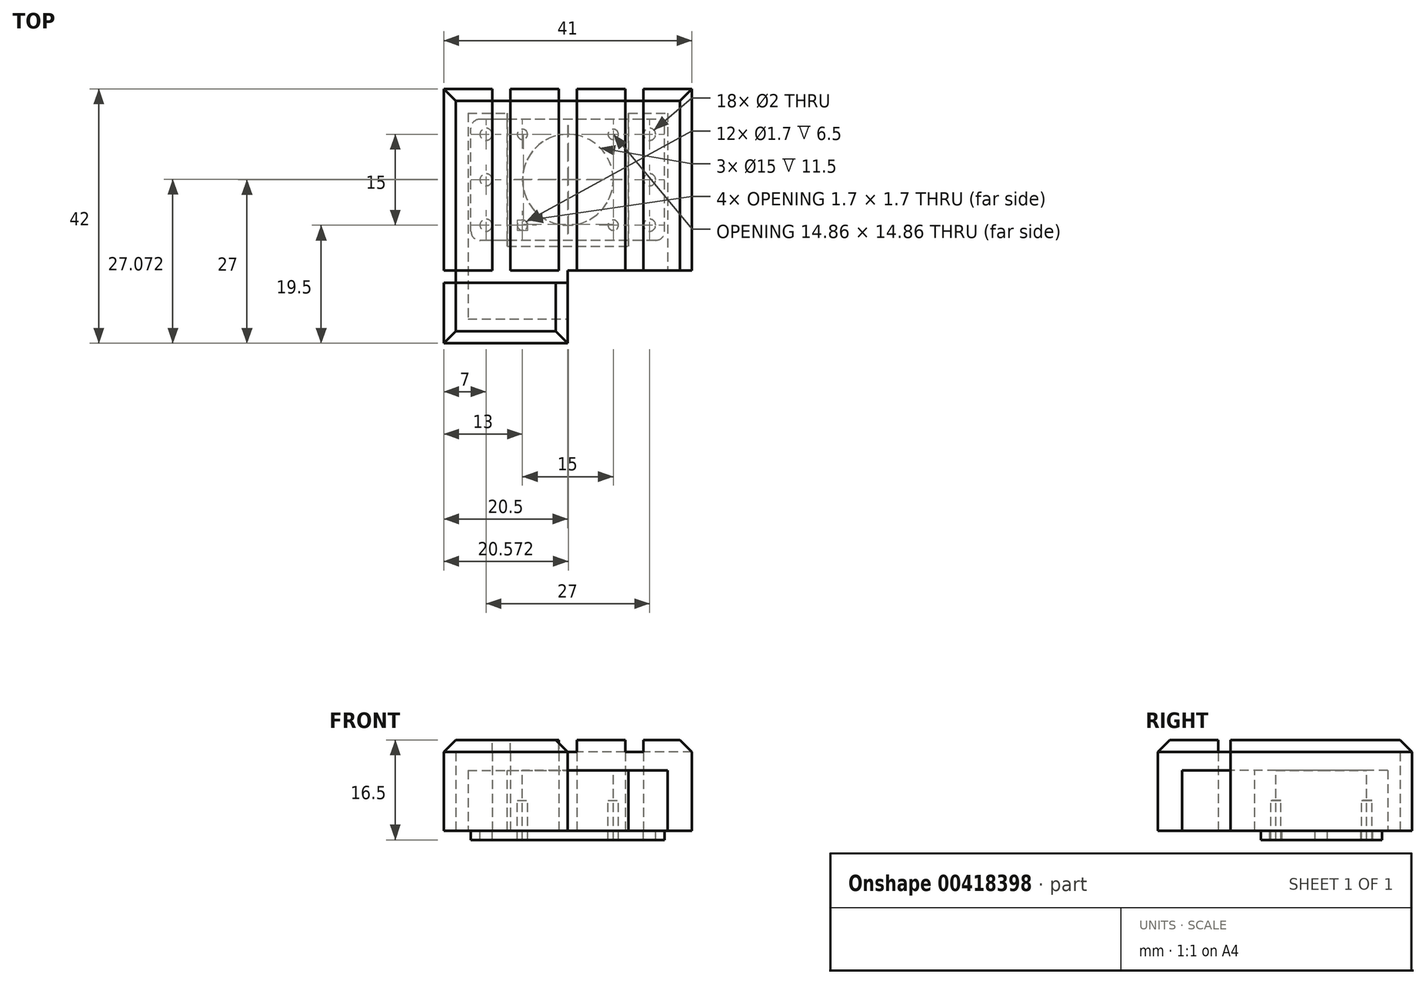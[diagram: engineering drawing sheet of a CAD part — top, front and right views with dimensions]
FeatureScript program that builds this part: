
annotation { "Feature Type Name" : "Feature", "Feature Type Description" : "" }
export const myFeature = defineFeature(function(context is Context, id is Id, definition is map)
    precondition{}
    {
        {
            var Q0;
            Q0=qCreatedBy(makeId("Top.planeOp"),FACE);
            var sketch = newSketch(context, id + "F0", { "sketchPlane" : qUnion([Q0])});
            skLineSegment(sketch, "E0.bottom", {"start": v(-20.5, 15) * mm, "end": v(20.5, 15) * mm});
            skLineSegment(sketch, "E0.top", {"start": v(-20.5, -15) * mm, "end": v(20.5, -15) * mm});
            skLineSegment(sketch, "E0.left", {"start": v(-20.5, 15) * mm, "end": v(-20.5, -15) * mm});
            skLineSegment(sketch, "E0.right", {"start": v(20.5, 15) * mm, "end": v(20.5, -15) * mm});
            skPoint(sketch, "E0.middle", {"position": v(0, 0) * mm});
            skLineSegment(sketch, "E1", {"start": v(-12.5, 15) * mm, "end": v(-12.5, -15) * mm});
            skLineSegment(sketch, "E2", {"start": v(-9.5, 15) * mm, "end": v(-9.5, -15) * mm});
            skLineSegment(sketch, "E3.MirrorCS", {"start": v(12.5, 15) * mm, "end": v(12.5, -15) * mm});
            skLineSegment(sketch, "E4.MirrorCS", {"start": v(9.5, 15) * mm, "end": v(9.5, -15) * mm});
            skLineSegment(sketch, "E5", {"start": v(-1.5, 15) * mm, "end": v(-1.5, -15) * mm});
            skLineSegment(sketch, "E6.MirrorCS", {"start": v(1.5, 15) * mm, "end": v(1.5, -15) * mm});
            skLineSegment(sketch, "E7", {"start": v(0, -15) * mm, "end": v(0, -27) * mm});
            skLineSegment(sketch, "E8", {"start": v(0, -27) * mm, "end": v(20.5, -27) * mm});
            skLineSegment(sketch, "E9", {"start": v(20.5, -27) * mm, "end": v(20.5, -15) * mm});
            skLineSegment(sketch, "E10", {"start": v(0, -17) * mm, "end": v(20.5, -17) * mm});
            skSolve(sketch);
        }
        {
            var Q0;
            Q0=qSketchRegion(id+"F0",true);
            extrude(context, id + "F1", {"entities" : qUnion([Q0]), "oppositeDirection" : true, "depth" : 15 * mm, "offsetDistance" : 25 * mm});
        }
        {
            var Q0;
            {var subQ0=sQuery(id+"F0.wireOp",EDGE,"E1");Q0=makeQuery(id+"F0.imprint","IMPRINT",FACE,{"disambiguationData":[TD([[makeQuery(id+"F0.imprint","IMPRINT",EDGE,{"derivedFrom":subQ0}),1.0]])]});}
            var Q1;
            {var subQ0=sQuery(id+"F0.wireOp",EDGE,"E5");Q1=makeQuery(id+"F0.imprint","IMPRINT",FACE,{"disambiguationData":[TD([[makeQuery(id+"F0.imprint","IMPRINT",EDGE,{"derivedFrom":subQ0}),1.0]])]});}
            var Q2;
            {var subQ0=sQuery(id+"F0.wireOp",EDGE,"E3.MirrorCS");Q2=makeQuery(id+"F0.imprint","IMPRINT",FACE,{"disambiguationData":[TD([[makeQuery(id+"F0.imprint","IMPRINT",EDGE,{"derivedFrom":subQ0}),-1.0]])]});}
            var Q3;
            {var subQ8=sQuery(id+"F0.wireOp",EDGE,"E10");Q3=makeQuery(id+"F0.imprint","IMPRINT",FACE,{"disambiguationData":[TD([[makeQuery(id+"F0.imprint","IMPRINT",EDGE,{"derivedFrom":subQ8}),1.0]])]});}
            extrude(context, id + "F2", {"entities" : qUnion([Q0, Q1, Q2, Q3]), "operationType" : NewBodyOperationType.REMOVE, "oppositeDirection" : true, "depth" : 2 * mm, "offsetDistance" : 25 * mm});
        }
        {
            var Q0;
            {var subQ0=sQuery(id+"F0.wireOp",EDGE,"E0.bottom");var subQ1=sQuery(id+"F0.wireOp",EDGE,"E0.left");Q0=makeQuery(id+"F2.boolean.opBoolean","SPLIT",EDGE,{"disambiguationData":[TD([makeQuery(id+"F1.opExtrude","SWEPT_FACE",FACE,{"disambiguationData":[OSD([subQ1])]})])],"derivedFrom":makeQuery(id+"F1.opExtrude","CAP_EDGE",EDGE,{"disambiguationData":[OSD([subQ0])],"isStart":true})});}
            var Q1;
            Q1=makeQuery(id+"F1.opExtrude","CAP_EDGE",EDGE,{"disambiguationData":[OSD([sQuery(id+"F0.wireOp",EDGE,"E0.left")])],"isStart":true});
            var Q2;
            {var subQ0=sQuery(id+"F0.wireOp",EDGE,"E0.bottom");var subQ1=sQuery(id+"F0.wireOp",EDGE,"E9");var subQ2=sQuery(id+"F0.wireOp",EDGE,"E0.right");Q2=makeQuery(id+"F2.boolean.opBoolean","SPLIT",EDGE,{"disambiguationData":[TD([makeQuery(id+"F1.opExtrude","SWEPT_FACE",FACE,{"disambiguationData":[OSD([subQ0])]})])],"derivedFrom":makeQuery(id+"F1.opExtrude","CAP_EDGE",EDGE,{"disambiguationData":[OSD([subQ2,subQ1])],"isStart":true})});}
            var Q3;
            {var subQ0=sQuery(id+"F0.wireOp",EDGE,"E0.bottom");Q3=makeQuery(id+"F2.boolean.opBoolean","SPLIT",EDGE,{"disambiguationData":[TD([makeQuery(id+"F2.opExtrude","SWEPT_FACE",FACE,{"disambiguationData":[OSD([sQuery(id+"F0.wireOp",EDGE,"E3.MirrorCS")])]})])],"derivedFrom":makeQuery(id+"F1.opExtrude","CAP_EDGE",EDGE,{"disambiguationData":[OSD([subQ0])],"isStart":true})});}
            var Q4;
            {var subQ0=sQuery(id+"F0.wireOp",EDGE,"E0.bottom");Q4=makeQuery(id+"F2.boolean.opBoolean","SPLIT",EDGE,{"disambiguationData":[TD([makeQuery(id+"F2.opExtrude","SWEPT_FACE",FACE,{"disambiguationData":[OSD([sQuery(id+"F0.wireOp",EDGE,"E4.MirrorCS")])]})])],"derivedFrom":makeQuery(id+"F1.opExtrude","CAP_EDGE",EDGE,{"disambiguationData":[OSD([subQ0])],"isStart":true})});}
            var Q5;
            {var subQ0=sQuery(id+"F0.wireOp",EDGE,"E0.bottom");Q5=makeQuery(id+"F2.boolean.opBoolean","SPLIT",EDGE,{"disambiguationData":[TD([makeQuery(id+"F2.opExtrude","SWEPT_FACE",FACE,{"disambiguationData":[OSD([sQuery(id+"F0.wireOp",EDGE,"E2")])]})])],"derivedFrom":makeQuery(id+"F1.opExtrude","CAP_EDGE",EDGE,{"disambiguationData":[OSD([subQ0])],"isStart":true})});}
            var Q6;
            Q6=makeQuery(id+"F1.opExtrude","CAP_EDGE",EDGE,{"disambiguationData":[OSD([sQuery(id+"F0.wireOp",EDGE,"E8")])],"isStart":true});
            var Q7;
            {var subQ0=sQuery(id+"F0.wireOp",EDGE,"E9");var subQ1=sQuery(id+"F0.wireOp",EDGE,"E8");var subQ2=sQuery(id+"F0.wireOp",EDGE,"E0.right");Q7=makeQuery(id+"F2.boolean.opBoolean","SPLIT",EDGE,{"disambiguationData":[TD([makeQuery(id+"F1.opExtrude","SWEPT_FACE",FACE,{"disambiguationData":[OSD([subQ1])]})])],"derivedFrom":makeQuery(id+"F1.opExtrude","CAP_EDGE",EDGE,{"disambiguationData":[OSD([subQ2,subQ0])],"isStart":true})});}
            var Q8;
            Q8=makeQuery(id+"F1.opExtrude","CAP_EDGE",EDGE,{"disambiguationData":[OSD([sQuery(id+"F0.wireOp",EDGE,"E7")])],"isStart":true});
            chamfer(context, id + "F3", {"entities" : qUnion([Q0, Q1, Q2, Q3, Q4, Q5, Q6, Q7, Q8]), "width" : 2 * mm, "tangentPropagation" : true});
        }
        {
            var Q0;
            {var subQ0=sQuery(id+"F0.wireOp",EDGE,"E0.bottom");var subQ1=sQuery(id+"F0.wireOp",EDGE,"E4.MirrorCS");var subQ2=sQuery(id+"F0.wireOp",EDGE,"E0.top");Q0=makeQuery(id+"F2.boolean.opBoolean","SPLIT",FACE,{"disambiguationData":[TD([makeQuery(id+"F2.opExtrude","SWEPT_FACE",FACE,{"disambiguationData":[OSD([subQ1])]})])],"derivedFrom":makeQuery(id+"F1.opExtrude","CAP_FACE",FACE,{"disambiguationData":[OSD([subQ0,subQ2,sQuery(id+"F0.wireOp",EDGE,"E0.left"),sQuery(id+"F0.wireOp",EDGE,"E0.right"),sQuery(id+"F0.wireOp",EDGE,"E7"),sQuery(id+"F0.wireOp",EDGE,"E8"),sQuery(id+"F0.wireOp",EDGE,"E9")])],"isStart":true})});}
            var sketch = newSketch(context, id + "F4", { "sketchPlane" : qUnion([Q0])});
            skCircle(sketch, "E11", {"center": v(-7.5, 7.5) * mm, "radius": 0.85 * mm});
            skCircle(sketch, "E12.MirrorC", {"center": v(7.5, 7.5) * mm, "radius": 0.85 * mm});
            skCircle(sketch, "E13.MirrorC", {"center": v(7.5, -7.5) * mm, "radius": 0.85 * mm});
            skCircle(sketch, "E14.MirrorC", {"center": v(-7.5, -7.5) * mm, "radius": 0.85 * mm});
            skSolve(sketch);
        }
        {
            var Q0;
            Q0=qSketchRegion(id+"F4",true);
            extrude(context, id + "F5", {"entities" : qUnion([Q0]), "operationType" : NewBodyOperationType.REMOVE, "endBound" : BoundingType.THROUGH_ALL, "oppositeDirection" : true, "depth" : 25 * mm, "offsetDistance" : 25 * mm});
        }
        {
            var Q0;
            Q0=makeQuery(id+"F1.opExtrude","CAP_FACE",FACE,{"disambiguationData":[OSD([sQuery(id+"F0.wireOp",EDGE,"E0.bottom"),sQuery(id+"F0.wireOp",EDGE,"E0.top"),sQuery(id+"F0.wireOp",EDGE,"E0.left"),sQuery(id+"F0.wireOp",EDGE,"E0.right"),sQuery(id+"F0.wireOp",EDGE,"E7"),sQuery(id+"F0.wireOp",EDGE,"E8"),sQuery(id+"F0.wireOp",EDGE,"E9")])],"isStart":false});
            var sketch = newSketch(context, id + "F6", { "sketchPlane" : qUnion([Q0])});
            skLineSegment(sketch, "E15.bottom", {"start": v(8.5, 16) * mm, "end": v(-8.5, 16) * mm});
            skLineSegment(sketch, "E15.top", {"start": v(8.5, -16) * mm, "end": v(-8.5, -16) * mm});
            skLineSegment(sketch, "E15.left", {"start": v(10, 14.5) * mm, "end": v(10, -14.5) * mm});
            skLineSegment(sketch, "E15.right", {"start": v(-10, 14.5) * mm, "end": v(-10, -14.5) * mm});
            skPoint(sketch, "E15.middle", {"position": v(0, 0) * mm});
            skCircle(sketch, "E16", {"center": v(0, 13.5) * mm, "radius": 1 * mm});
            skCircle(sketch, "E17", {"center": v(7.5, 13.5) * mm, "radius": 1 * mm});
            skCircle(sketch, "E18.MirrorC", {"center": v(-7.5, 13.5) * mm, "radius": 1 * mm});
            skCircle(sketch, "E19.MirrorC", {"center": v(7.5, -13.5) * mm, "radius": 1 * mm});
            skCircle(sketch, "E20.MirrorC", {"center": v(-7.5, -13.5) * mm, "radius": 1 * mm});
            skCircle(sketch, "E21.MirrorC", {"center": v(0, -13.5) * mm, "radius": 1 * mm});
            skPoint(sketch, "E22.visualSharp", {"position": v(10, 16) * mm});
            skArc(sketch, "E22.filletArc", {"start": v(10, 14.5) * mm, "mid": v(9.56, 15.56) * mm, "end": v(8.5, 16) * mm});
            skPoint(sketch, "E23.visualSharp", {"position": v(10, -16) * mm});
            skArc(sketch, "E23.filletArc", {"start": v(8.5, -16) * mm, "mid": v(9.56, -15.56) * mm, "end": v(10, -14.5) * mm});
            skPoint(sketch, "E24.visualSharp", {"position": v(-10, -16) * mm});
            skArc(sketch, "E24.filletArc", {"start": v(-10, -14.5) * mm, "mid": v(-9.56, -15.56) * mm, "end": v(-8.5, -16) * mm});
            skPoint(sketch, "E25.visualSharp", {"position": v(-10, 16) * mm});
            skArc(sketch, "E25.filletArc", {"start": v(-8.5, 16) * mm, "mid": v(-9.56, 15.56) * mm, "end": v(-10, 14.5) * mm});
            skCircle(sketch, "E26", {"center": v(0, 0) * mm, "radius": 7.5 * mm});
            skSolve(sketch);
        }
        {
            var Q0;
            Q0=qSketchRegion(id+"F6",true);
            extrude(context, id + "F7", {"entities" : qUnion([Q0]), "depth" : 1.5 * mm, "offsetDistance" : 25 * mm});
        }
        {
            var Q0;
            Q0=makeQuery(id+"F1.opExtrude","SWEPT_FACE",FACE,{"disambiguationData":[OSD([sQuery(id+"F0.wireOp",EDGE,"E0.bottom")])]});
            var sketch = newSketch(context, id + "F8", { "sketchPlane" : qUnion([Q0])});
            skLineSegment(sketch, "E27", {"start": v(12.5, -2) * mm, "end": v(12.5, -15) * mm});
            skLineSegment(sketch, "E28", {"start": v(9.5, -2) * mm, "end": v(9.5, -15) * mm});
            skLineSegment(sketch, "E29", {"start": v(9.5, -15) * mm, "end": v(12.5, -15) * mm});
            skLineSegment(sketch, "E30", {"start": v(12.5, -2) * mm, "end": v(9.5, -2) * mm});
            skLineSegment(sketch, "E31", {"start": v(1.5, -2) * mm, "end": v(1.5, -15) * mm});
            skLineSegment(sketch, "E32", {"start": v(1.5, -15) * mm, "end": v(0, -15) * mm});
            skLineSegment(sketch, "E33", {"start": v(1.5, -2) * mm, "end": v(0, -2) * mm});
            skLineSegment(sketch, "E34.MirrorCS", {"start": v(-1.5, -2) * mm, "end": v(0, -2) * mm});
            skLineSegment(sketch, "E35.MirrorCS", {"start": v(-1.5, -15) * mm, "end": v(0, -15) * mm});
            skLineSegment(sketch, "E36.MirrorCS", {"start": v(-9.5, -15) * mm, "end": v(-12.5, -15) * mm});
            skLineSegment(sketch, "E37.MirrorCS", {"start": v(-12.5, -2) * mm, "end": v(-12.5, -15) * mm});
            skLineSegment(sketch, "E38.MirrorCS", {"start": v(-1.5, -2) * mm, "end": v(-1.5, -15) * mm});
            skLineSegment(sketch, "E39.MirrorCS", {"start": v(-12.5, -2) * mm, "end": v(-9.5, -2) * mm});
            skLineSegment(sketch, "E40.MirrorCS", {"start": v(-9.5, -2) * mm, "end": v(-9.5, -15) * mm});
            skSolve(sketch);
        }
        {
            var Q0;
            Q0=qSketchRegion(id+"F8",true);
            extrude(context, id + "F9", {"entities" : qUnion([Q0]), "operationType" : NewBodyOperationType.REMOVE, "oppositeDirection" : true, "depth" : 2 * mm, "offsetDistance" : 25 * mm});
        }
        {
            var Q0;
            Q0=makeQuery(id+"F1.opExtrude","SWEPT_FACE",FACE,{"disambiguationData":[OSD([sQuery(id+"F0.wireOp",EDGE,"E0.right"),sQuery(id+"F0.wireOp",EDGE,"E9")])]});
            var sketch = newSketch(context, id + "F10", { "sketchPlane" : qUnion([Q0])});
            skLineSegment(sketch, "E41.bottom", {"start": v(-15, -2) * mm, "end": v(-17, -2) * mm});
            skLineSegment(sketch, "E41.top", {"start": v(-15, -15) * mm, "end": v(-17, -15) * mm});
            skLineSegment(sketch, "E41.left", {"start": v(-15, -2) * mm, "end": v(-15, -15) * mm});
            skLineSegment(sketch, "E41.right", {"start": v(-17, -2) * mm, "end": v(-17, -15) * mm});
            skSolve(sketch);
        }
        {
            var Q0;
            Q0=qSketchRegion(id+"F10",true);
            extrude(context, id + "F11", {"entities" : qUnion([Q0]), "operationType" : NewBodyOperationType.REMOVE, "oppositeDirection" : true, "depth" : 2 * mm, "offsetDistance" : 25 * mm});
        }
        {
            var Q0;
            Q0=makeQuery(id+"F7.opExtrude","SWEPT_BODY",BODY,{"disambiguationData":[OSD([sQuery(id+"F6.wireOp",EDGE,"E15.bottom"),sQuery(id+"F6.wireOp",EDGE,"E15.top"),sQuery(id+"F6.wireOp",EDGE,"E15.left"),sQuery(id+"F6.wireOp",EDGE,"E15.right"),sQuery(id+"F6.wireOp",EDGE,"E16"),sQuery(id+"F6.wireOp",EDGE,"E18.MirrorC"),sQuery(id+"F6.wireOp",EDGE,"E17"),sQuery(id+"F6.wireOp",EDGE,"E19.MirrorC"),sQuery(id+"F6.wireOp",EDGE,"E20.MirrorC"),sQuery(id+"F6.wireOp",EDGE,"E21.MirrorC"),sQuery(id+"F6.wireOp",EDGE,"E22.filletArc"),sQuery(id+"F6.wireOp",EDGE,"E23.filletArc"),sQuery(id+"F6.wireOp",EDGE,"E24.filletArc"),sQuery(id+"F6.wireOp",EDGE,"E25.filletArc"),sQuery(id+"F6.wireOp",EDGE,"E26")])]});
            var Q1;
            Q1=makeQuery(id+"F7.opExtrude","CAP_EDGE",EDGE,{"disambiguationData":[OSD([sQuery(id+"F6.wireOp",EDGE,"E26")])],"isStart":true});
            transform(context, id + "F12", {"entities" : qUnion([Q0]), "transformType" : TransformType.ROTATION, "transformAxis" : qUnion([Q1]), "angle" : 90 * degree, "makeCopy" : false});
        }
        {
            var Q0;
            Q0=makeQuery(id+"F7.opExtrude","CAP_FACE",FACE,{"disambiguationData":[OSD([sQuery(id+"F6.wireOp",EDGE,"E15.bottom"),sQuery(id+"F6.wireOp",EDGE,"E15.top"),sQuery(id+"F6.wireOp",EDGE,"E15.left"),sQuery(id+"F6.wireOp",EDGE,"E15.right"),sQuery(id+"F6.wireOp",EDGE,"E16"),sQuery(id+"F6.wireOp",EDGE,"E18.MirrorC"),sQuery(id+"F6.wireOp",EDGE,"E17"),sQuery(id+"F6.wireOp",EDGE,"E19.MirrorC"),sQuery(id+"F6.wireOp",EDGE,"E20.MirrorC"),sQuery(id+"F6.wireOp",EDGE,"E21.MirrorC"),sQuery(id+"F6.wireOp",EDGE,"E22.filletArc"),sQuery(id+"F6.wireOp",EDGE,"E23.filletArc"),sQuery(id+"F6.wireOp",EDGE,"E24.filletArc"),sQuery(id+"F6.wireOp",EDGE,"E25.filletArc"),sQuery(id+"F6.wireOp",EDGE,"E26")])],"isStart":false});
            var sketch = newSketch(context, id + "F13", { "sketchPlane" : qUnion([Q0])});
            skCircle(sketch, "E42.0", {"center": v(-7.5, -7.5) * mm, "radius": 0.85 * mm});
            skCircle(sketch, "E43.0", {"center": v(7.5, -7.5) * mm, "radius": 0.85 * mm});
            skCircle(sketch, "E44.0", {"center": v(-7.5, 7.5) * mm, "radius": 0.85 * mm});
            skCircle(sketch, "E45.0", {"center": v(7.5, 7.5) * mm, "radius": 0.85 * mm});
            skSolve(sketch);
        }
        {
            var Q0;
            Q0=qSketchRegion(id+"F13",true);
            extrude(context, id + "F14", {"entities" : qUnion([Q0]), "operationType" : NewBodyOperationType.REMOVE, "endBound" : BoundingType.UP_TO_NEXT, "oppositeDirection" : true, "depth" : 25 * mm, "offsetDistance" : 25 * mm});
        }
        {
            var Q0;
            Q0=makeQuery(id+"F1.opExtrude","CAP_FACE",FACE,{"disambiguationData":[OSD([sQuery(id+"F0.wireOp",EDGE,"E0.bottom"),sQuery(id+"F0.wireOp",EDGE,"E0.top"),sQuery(id+"F0.wireOp",EDGE,"E0.left"),sQuery(id+"F0.wireOp",EDGE,"E0.right"),sQuery(id+"F0.wireOp",EDGE,"E7"),sQuery(id+"F0.wireOp",EDGE,"E8"),sQuery(id+"F0.wireOp",EDGE,"E9")])],"isStart":false});
            var sketch = newSketch(context, id + "F15", { "sketchPlane" : qUnion([Q0])});
            skLineSegment(sketch, "E46.bottom", {"start": v(16.5, -11) * mm, "end": v(-16.5, -11) * mm});
            skLineSegment(sketch, "E46.top", {"start": v(16.5, 23) * mm, "end": v(-16.5, 23) * mm});
            skLineSegment(sketch, "E46.left", {"start": v(16.5, -11) * mm, "end": v(16.5, 23) * mm});
            skLineSegment(sketch, "E46.right", {"start": v(-16.5, -11) * mm, "end": v(-16.5, 23) * mm});
            skSolve(sketch);
        }
        {
            var Q0;
            Q0=qSketchRegion(id+"F15",true);
            extrude(context, id + "F16", {"entities" : qUnion([Q0]), "operationType" : NewBodyOperationType.REMOVE, "oppositeDirection" : true, "depth" : 10 * mm, "offsetDistance" : 25 * mm});
        }
        {
            var Q0;
            Q0=makeQuery(id+"F16.boolean.opBoolean","COPY",FACE,{"derivedFrom":makeQuery(id+"F16.opExtrude","CAP_FACE",FACE,{"disambiguationData":[OSD([sQuery(id+"F15.wireOp",EDGE,"E46.bottom"),sQuery(id+"F15.wireOp",EDGE,"E46.top"),sQuery(id+"F15.wireOp",EDGE,"E46.left"),sQuery(id+"F15.wireOp",EDGE,"E46.right")])],"isStart":false})});
            var sketch = newSketch(context, id + "F17", { "sketchPlane" : qUnion([Q0])});
            skLineSegment(sketch, "E47.bottom", {"start": v(10, -11) * mm, "end": v(-10, -11) * mm});
            skLineSegment(sketch, "E47.top", {"start": v(10, 11) * mm, "end": v(-10, 11) * mm});
            skLineSegment(sketch, "E47.left", {"start": v(10, -11) * mm, "end": v(10, 11) * mm});
            skLineSegment(sketch, "E47.right", {"start": v(-10, -11) * mm, "end": v(-10, 11) * mm});
            skPoint(sketch, "E47.middle", {"position": v(0, 0) * mm});
            skPoint(sketch, "E48", {"position": v(7.5, 7.5) * mm});
            skCircle(sketch, "E49.0", {"center": v(7.5, -7.5) * mm, "radius": 0.85 * mm});
            skCircle(sketch, "E50.0", {"center": v(-7.5, -7.5) * mm, "radius": 0.85 * mm});
            skCircle(sketch, "E51.0", {"center": v(-7.5, 7.5) * mm, "radius": 0.85 * mm});
            skCircle(sketch, "E52.0", {"center": v(7.5, 7.5) * mm, "radius": 0.85 * mm});
            skCircle(sketch, "E53", {"center": v(0, 0) * mm, "radius": 7.5 * mm});
            skSolve(sketch);
        }
        {
            var Q0;
            Q0=qSketchRegion(id+"F17",true);
            var Q1;
            Q1=makeQuery(id+"F1.opExtrude","CAP_FACE",FACE,{"disambiguationData":[OSD([sQuery(id+"F0.wireOp",EDGE,"E0.bottom"),sQuery(id+"F0.wireOp",EDGE,"E0.top"),sQuery(id+"F0.wireOp",EDGE,"E0.left"),sQuery(id+"F0.wireOp",EDGE,"E0.right"),sQuery(id+"F0.wireOp",EDGE,"E7"),sQuery(id+"F0.wireOp",EDGE,"E8"),sQuery(id+"F0.wireOp",EDGE,"E9")])],"isStart":false});
            extrude(context, id + "F18", {"entities" : qUnion([Q0]), "operationType" : NewBodyOperationType.ADD, "endBound" : BoundingType.UP_TO_SURFACE, "depth" : 25 * mm, "endBoundEntityFace" : qUnion([Q1]), "offsetDistance" : 25 * mm});
        }
        {
            var Q0;
            {var subQ0=sQuery(id+"F0.wireOp",EDGE,"E0.bottom");var subQ1=sQuery(id+"F0.wireOp",EDGE,"E0.top");Q0=makeQuery(id+"F2.boolean.opBoolean","SPLIT",FACE,{"disambiguationData":[TD([makeQuery(id+"F2.opExtrude","SWEPT_FACE",FACE,{"disambiguationData":[OSD([sQuery(id+"F0.wireOp",EDGE,"E2")])]})])],"derivedFrom":makeQuery(id+"F1.opExtrude","CAP_FACE",FACE,{"disambiguationData":[OSD([subQ0,subQ1,sQuery(id+"F0.wireOp",EDGE,"E0.left"),sQuery(id+"F0.wireOp",EDGE,"E0.right"),sQuery(id+"F0.wireOp",EDGE,"E7"),sQuery(id+"F0.wireOp",EDGE,"E8"),sQuery(id+"F0.wireOp",EDGE,"E9")])],"isStart":true})});}
            var sketch = newSketch(context, id + "F19", { "sketchPlane" : qUnion([Q0])});
            skCircle(sketch, "E54.0", {"center": v(7.5, 7.5) * mm, "radius": 0.85 * mm});
            skCircle(sketch, "E55.0", {"center": v(-7.5, 7.5) * mm, "radius": 0.85 * mm});
            skCircle(sketch, "E56.0", {"center": v(-7.5, -7.5) * mm, "radius": 0.85 * mm});
            skCircle(sketch, "E57.0", {"center": v(7.5, -7.5) * mm, "radius": 0.85 * mm});
            skSolve(sketch);
        }
        {
            var Q0;
            Q0=qSketchRegion(id+"F19",true);
            extrude(context, id + "F20", {"entities" : qUnion([Q0]), "operationType" : NewBodyOperationType.ADD, "oppositeDirection" : true, "depth" : 10 * mm, "offsetDistance" : 25 * mm});
        }
        {
            var Q0;
            Q0=qCreatedBy(makeId("Right.planeOp"),FACE);
            cPlane(context, id + "F21", {"entities" : qUnion([Q0]), "cplaneType" : CPlaneType.OFFSET, "offset" : 30 * mm, "oppositeDirection" : true, "width" : 150 * mm, "height" : 150 * mm});
        }
        {
            var Q0;
            Q0=makeQuery(id+"F1.opExtrude","SWEPT_BODY",BODY,{"disambiguationData":[OSD([sQuery(id+"F0.wireOp",EDGE,"E0.bottom"),sQuery(id+"F0.wireOp",EDGE,"E0.top"),sQuery(id+"F0.wireOp",EDGE,"E0.left"),sQuery(id+"F0.wireOp",EDGE,"E0.right"),sQuery(id+"F0.wireOp",EDGE,"E7"),sQuery(id+"F0.wireOp",EDGE,"E8"),sQuery(id+"F0.wireOp",EDGE,"E9")])]});
            var Q1;
            Q1=qCreatedBy(id+"F21.planeOp",FACE);
            mirror(context, id + "F22", {"entities" : qUnion([Q0]), "mirrorPlane" : qUnion([Q1])});
        }
        {
            var Q0;
            Q0=makeQuery(id+"F7.opExtrude","SWEPT_BODY",BODY,{"disambiguationData":[OSD([sQuery(id+"F6.wireOp",EDGE,"E15.bottom"),sQuery(id+"F6.wireOp",EDGE,"E15.top"),sQuery(id+"F6.wireOp",EDGE,"E15.left"),sQuery(id+"F6.wireOp",EDGE,"E15.right"),sQuery(id+"F6.wireOp",EDGE,"E16"),sQuery(id+"F6.wireOp",EDGE,"E18.MirrorC"),sQuery(id+"F6.wireOp",EDGE,"E17"),sQuery(id+"F6.wireOp",EDGE,"E19.MirrorC"),sQuery(id+"F6.wireOp",EDGE,"E20.MirrorC"),sQuery(id+"F6.wireOp",EDGE,"E21.MirrorC"),sQuery(id+"F6.wireOp",EDGE,"E22.filletArc"),sQuery(id+"F6.wireOp",EDGE,"E23.filletArc"),sQuery(id+"F6.wireOp",EDGE,"E24.filletArc"),sQuery(id+"F6.wireOp",EDGE,"E25.filletArc"),sQuery(id+"F6.wireOp",EDGE,"E26")])]});
            var Q1;
            Q1=makeQuery(id+"F1.opExtrude","SWEPT_BODY",BODY,{"disambiguationData":[OSD([sQuery(id+"F0.wireOp",EDGE,"E0.bottom"),sQuery(id+"F0.wireOp",EDGE,"E0.top"),sQuery(id+"F0.wireOp",EDGE,"E0.left"),sQuery(id+"F0.wireOp",EDGE,"E0.right"),sQuery(id+"F0.wireOp",EDGE,"E7"),sQuery(id+"F0.wireOp",EDGE,"E8"),sQuery(id+"F0.wireOp",EDGE,"E9")])]});
            deleteBodies(context, id + "F23", {"entities" : qUnion([Q0, Q1])});
        }
    });
